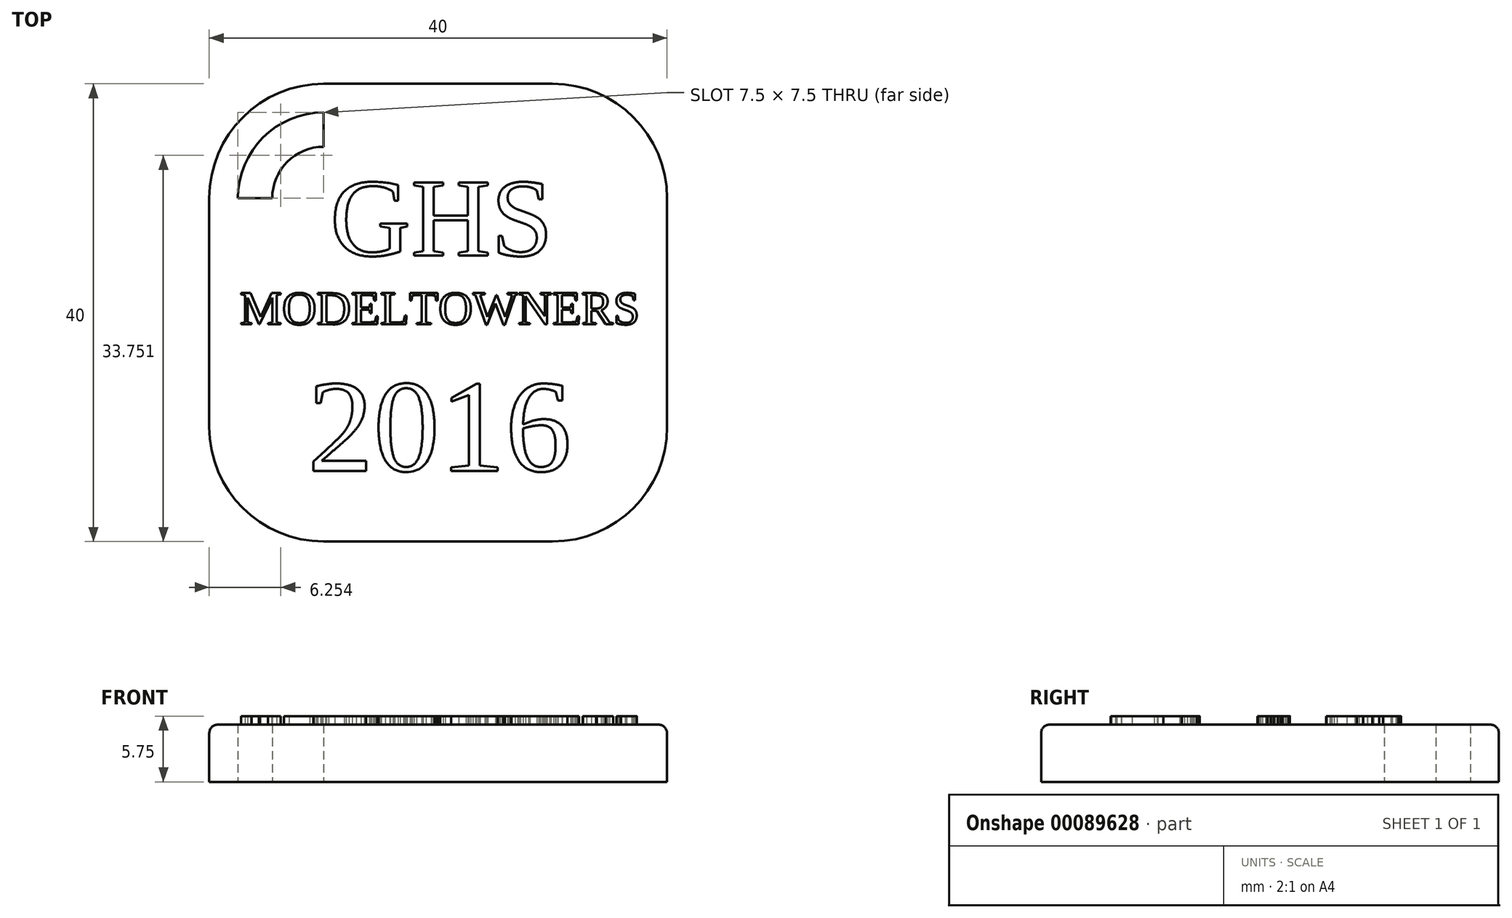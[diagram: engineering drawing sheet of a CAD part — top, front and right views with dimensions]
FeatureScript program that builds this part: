
annotation { "Feature Type Name" : "Feature", "Feature Type Description" : "" }
export const myFeature = defineFeature(function(context is Context, id is Id, definition is map)
    precondition{}
    {
        {
            var Q0;
            Q0=qCreatedBy(makeId("Top.planeOp"),FACE);
            var sketch = newSketch(context, id + "F0", { "sketchPlane" : qUnion([Q0])});
            skLineSegment(sketch, "E0.bottom", {"start": v(-73.67, 40.7) * mm, "end": v(-53.67, 40.7) * mm});
            skLineSegment(sketch, "E0.top", {"start": v(-73.67, 0.7) * mm, "end": v(-53.67, 0.7) * mm});
            skLineSegment(sketch, "E0.left", {"start": v(-83.67, 30.7) * mm, "end": v(-83.67, 10.7) * mm});
            skLineSegment(sketch, "E0.right", {"start": v(-43.67, 30.7) * mm, "end": v(-43.67, 10.7) * mm});
            skPoint(sketch, "E1.visualSharp", {"position": v(-83.67, 40.7) * mm});
            skArc(sketch, "E1.filletArc", {"start": v(-73.67, 40.7) * mm, "mid": v(-80.74, 37.77) * mm, "end": v(-83.67, 30.7) * mm});
            skPoint(sketch, "E2.visualSharp", {"position": v(-43.67, 40.7) * mm});
            skArc(sketch, "E2.filletArc", {"start": v(-43.67, 30.7) * mm, "mid": v(-46.6, 37.77) * mm, "end": v(-53.67, 40.7) * mm});
            skPoint(sketch, "E3.visualSharp", {"position": v(-43.67, 0.7) * mm});
            skArc(sketch, "E3.filletArc", {"start": v(-53.67, 0.7) * mm, "mid": v(-46.6, 3.63) * mm, "end": v(-43.67, 10.7) * mm});
            skPoint(sketch, "E4.visualSharp", {"position": v(-83.67, 0.7) * mm});
            skArc(sketch, "E4.filletArc", {"start": v(-83.67, 10.7) * mm, "mid": v(-80.74, 3.63) * mm, "end": v(-73.67, 0.7) * mm});
            skPoint(sketch, "E5.visualSharp", {"position": v(-81.17, 38.2) * mm});
            skArc(sketch, "E5.filletArc", {"start": v(-73.67, 38.2) * mm, "mid": v(-78.97, 36) * mm, "end": v(-81.17, 30.7) * mm});
            skArc(sketch, "E6.1", {"start": v(-73.67, 35.2) * mm, "mid": v(-76.85, 33.88) * mm, "end": v(-78.17, 30.7) * mm});
            skLineSegment(sketch, "E7", {"start": v(-73.67, 38.2) * mm, "end": v(-73.67, 35.2) * mm});
            skLineSegment(sketch, "E8", {"start": v(-78.17, 30.7) * mm, "end": v(-81.17, 30.7) * mm});
            skSolve(sketch);
        }
        {
            var Q0;
            Q0 = qSketchRegion(id + "F0", true);
            extrude(context, id + "F1", {"entities" : qUnion([Q0]), "depth" : 5 * mm});
        }
        {
            var Q0;
            Q0=makeQuery(id+"F1.opExtrude","CAP_FACE",FACE,{"disambiguationData":[OSD([sQuery(id+"F0.wireOp",EDGE,"E0.bottom"),sQuery(id+"F0.wireOp",EDGE,"E0.top"),sQuery(id+"F0.wireOp",EDGE,"E0.left"),sQuery(id+"F0.wireOp",EDGE,"E0.right"),sQuery(id+"F0.wireOp",EDGE,"E1.filletArc"),sQuery(id+"F0.wireOp",EDGE,"E2.filletArc"),sQuery(id+"F0.wireOp",EDGE,"E3.filletArc"),sQuery(id+"F0.wireOp",EDGE,"E4.filletArc"),sQuery(id+"F0.wireOp",EDGE,"E5.filletArc"),sQuery(id+"F0.wireOp",EDGE,"E6.1"),sQuery(id+"F0.wireOp",EDGE,"E7"),sQuery(id+"F0.wireOp",EDGE,"E8")])],"isStart":false});
            var sketch = newSketch(context, id + "F2", { "sketchPlane" : qUnion([Q0])});
            skPoint(sketch, "E9.centerSnap0", {"position": v(-63.67, 40.7) * mm});
            skPoint(sketch, "E9.centerSnap1", {"position": v(-43.67, 20.7) * mm});
            skText(sketch, "E10", { "text": "GHS", "fontName": "Tinos-Regular.ttf"});
            skText(sketch, "E11", { "text": "MODELTOWNERS", "fontName": "Tinos-Regular.ttf"});
            skText(sketch, "E12", { "text": "2016", "fontName": "Tinos-Regular.ttf"});
            const initialGuessF2  = {"E10": [-0.07309, 0.0257, 1, 0, 0.007], "E11": [-0.08101, 0.01968, 1, 0, 0.003], "E12": [-0.07508, 0.00688, 1, 0, 0.0083]};
            skSetInitialGuess(sketch, initialGuessF2);
            skSolve(sketch);
        }
        {
            var Q0;
            Q0 = qSketchRegion(id + "F2", true);
            extrude(context, id + "F3", {"entities" : qUnion([Q0]), "operationType" : NewBodyOperationType.ADD, "depth" : 0.75 * mm});
        }
        {
            var Q0;
            Q0=makeQuery(id+"F1.opExtrude","CAP_EDGE",EDGE,{"disambiguationData":[OSD([sQuery(id+"F0.wireOp",EDGE,"E0.left")])],"isStart":false});
            var Q1;
            Q1=makeQuery(id+"F1.opExtrude","CAP_EDGE",EDGE,{"disambiguationData":[OSD([sQuery(id+"F0.wireOp",EDGE,"E4.filletArc")])],"isStart":false});
            var Q2;
            Q2=makeQuery(id+"F1.opExtrude","CAP_EDGE",EDGE,{"disambiguationData":[OSD([sQuery(id+"F0.wireOp",EDGE,"E0.top")])],"isStart":false});
            var Q3;
            Q3=makeQuery(id+"F1.opExtrude","CAP_EDGE",EDGE,{"disambiguationData":[OSD([sQuery(id+"F0.wireOp",EDGE,"E3.filletArc")])],"isStart":false});
            var Q4;
            Q4=makeQuery(id+"F1.opExtrude","CAP_EDGE",EDGE,{"disambiguationData":[OSD([sQuery(id+"F0.wireOp",EDGE,"E0.right")])],"isStart":false});
            var Q5;
            Q5=makeQuery(id+"F1.opExtrude","CAP_EDGE",EDGE,{"disambiguationData":[OSD([sQuery(id+"F0.wireOp",EDGE,"E2.filletArc")])],"isStart":false});
            var Q6;
            Q6=makeQuery(id+"F1.opExtrude","CAP_EDGE",EDGE,{"disambiguationData":[OSD([sQuery(id+"F0.wireOp",EDGE,"E0.bottom")])],"isStart":false});
            var Q7;
            Q7=makeQuery(id+"F1.opExtrude","CAP_EDGE",EDGE,{"disambiguationData":[OSD([sQuery(id+"F0.wireOp",EDGE,"E1.filletArc")])],"isStart":false});
            fillet(context, id + "F4", {"entities" : qUnion([Q0, Q1, Q2, Q3, Q4, Q5, Q6, Q7]), "radius" : 0.75 * mm, "tangentPropagation" : true, "allowEdgeOverflow" : false});
        }
    });
